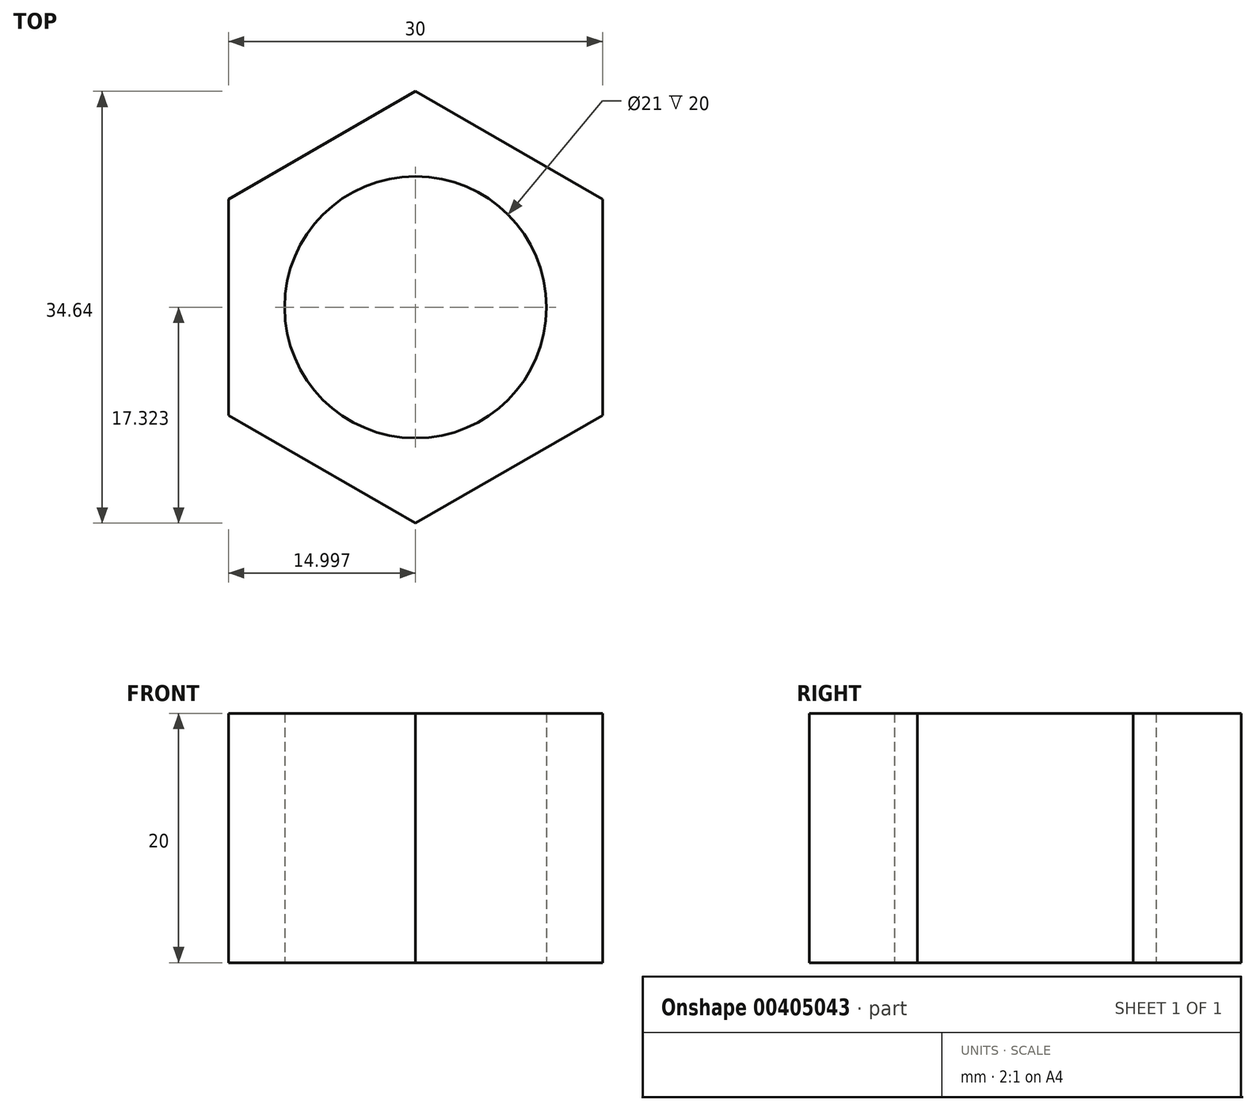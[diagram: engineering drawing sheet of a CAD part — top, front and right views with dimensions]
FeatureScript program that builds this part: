
annotation { "Feature Type Name" : "Feature", "Feature Type Description" : "" }
export const myFeature = defineFeature(function(context is Context, id is Id, definition is map)
    precondition{}
    {
        {
            var Q0;
            Q0=qCreatedBy(makeId("Top.planeOp"),FACE);
            var sketch = newSketch(context, id + "F0", { "sketchPlane" : qUnion([Q0])});
            skCircle(sketch, "E0.cCircle", {"center": v(-0.83, 1.44) * mm, "radius": 15 * mm, "construction": true});
            skLineSegment(sketch, "E0.0", {"start": v(14.17, -7.22) * mm, "end": v(-0.83, -15.88) * mm});
            skLineSegment(sketch, "E0.1", {"start": v(-0.83, -15.88) * mm, "end": v(-15.83, -7.22) * mm});
            skLineSegment(sketch, "E0.2", {"start": v(-15.83, -7.22) * mm, "end": v(-15.83, 10.1) * mm});
            skLineSegment(sketch, "E0.3", {"start": v(-15.83, 10.1) * mm, "end": v(-0.83, 18.76) * mm});
            skLineSegment(sketch, "E0.4", {"start": v(-0.83, 18.76) * mm, "end": v(14.17, 10.1) * mm});
            skLineSegment(sketch, "E0.5", {"start": v(14.17, 10.1) * mm, "end": v(14.17, -7.22) * mm});
            skPoint(sketch, "E0.0.midPoint", {"position": v(6.67, -11.55) * mm});
            skCircle(sketch, "E1", {"center": v(-0.83, 1.44) * mm, "radius": 10.5 * mm});
            skSolve(sketch);
        }
        {
            var Q0;
            Q0=makeQuery(id+"F0.imprint","IMPRINT",FACE,{"disambiguationData":[TD([[makeQuery(id+"F0.imprint","IMPRINT",EDGE,{"derivedFrom":sQuery(id+"F0.wireOp",EDGE,"E0.0")}),-1.0]])]});
            extrude(context, id + "F1", {"entities" : qUnion([Q0]), "depth" : 20 * mm});
        }
    });
